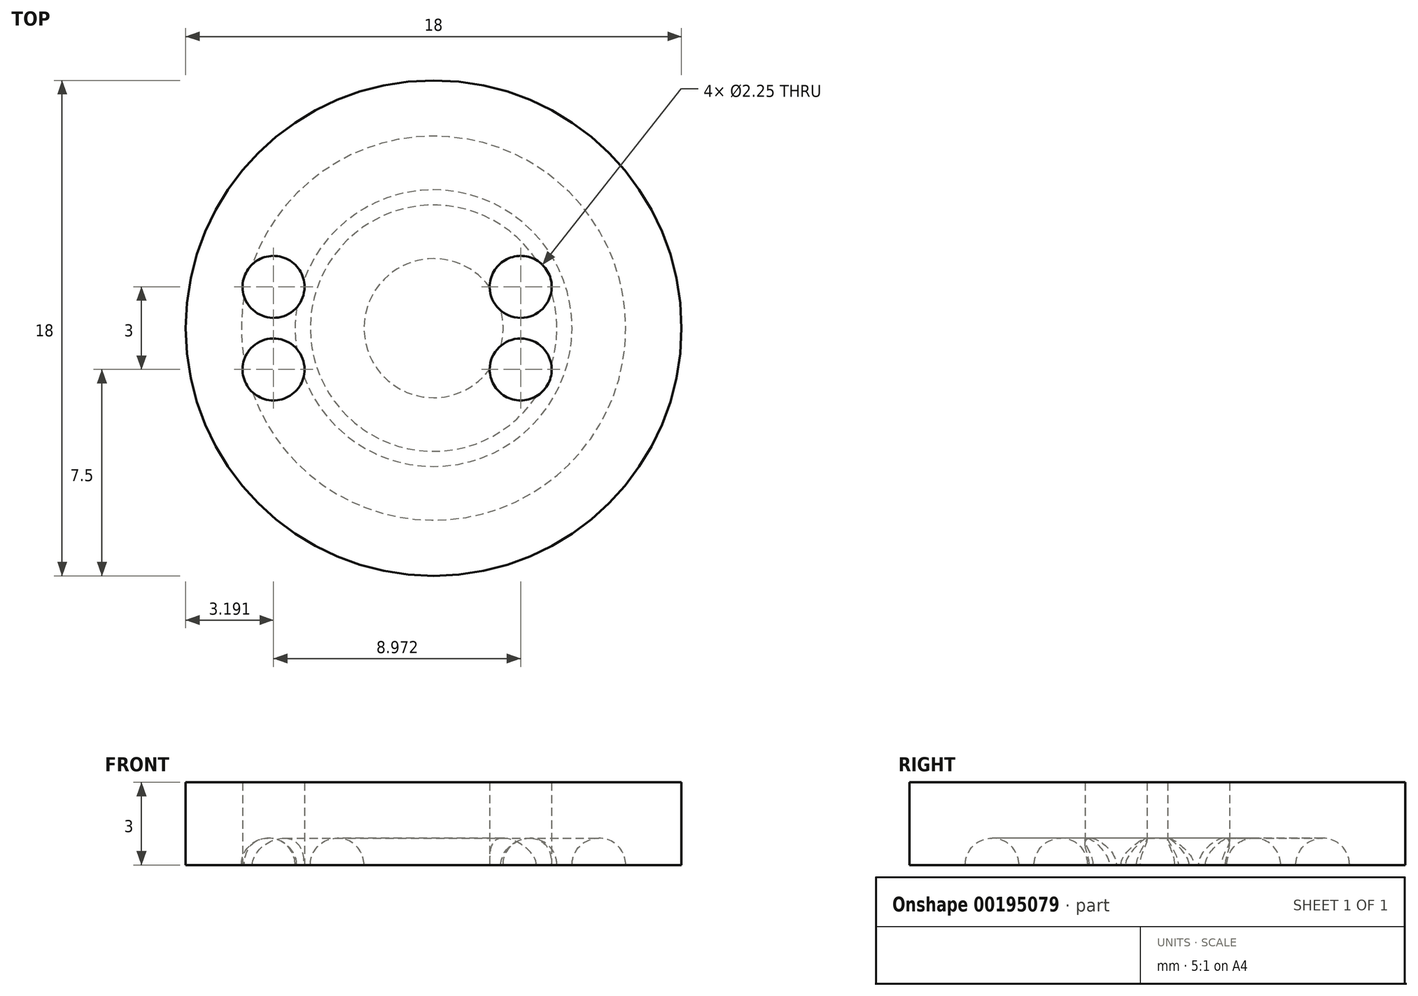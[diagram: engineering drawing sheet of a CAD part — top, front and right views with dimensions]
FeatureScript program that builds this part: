
annotation { "Feature Type Name" : "Feature", "Feature Type Description" : "" }
export const myFeature = defineFeature(function(context is Context, id is Id, definition is map)
    precondition{}
    {
        {
            assignVariable(context, id + "F0", {"name" : "thick", "anyValue" : 3});
        }
        {
            var Q0;
            Q0=qCreatedBy(makeId("Top.planeOp"),FACE);
            var sketch = newSketch(context, id + "F1", { "sketchPlane" : qUnion([Q0])});
            skCircle(sketch, "E0", {"center": v(0, 0) * mm, "radius": 9 * mm});
            skSolve(sketch);
        }
        {
            var Q0;
            Q0=qSketchRegion(id+"F1",true);
            extrude(context, id + "F2", {"entities" : qUnion([Q0]), "depth" : (getVariable(context, 'thick')) * mm});
        }
        {
            var Q0;
            Q0=makeQuery(id+"F2.opExtrude","CAP_FACE",FACE,{"disambiguationData":[OSD([sQuery(id+"F1.wireOp",EDGE,"E0")])],"isStart":true});
            var sketch = newSketch(context, id + "F3", { "sketchPlane" : qUnion([Q0])});
            skCircle(sketch, "E1", {"center": v(0, 0) * mm, "radius": 6 * mm});
            skCircle(sketch, "E2", {"center": v(0, 0) * mm, "radius": 3.5 * mm});
            skSolve(sketch);
        }
        {
            var Q0;
            Q0=qCreatedBy(makeId("Front.planeOp"),FACE);
            var sketch = newSketch(context, id + "F4", { "sketchPlane" : qUnion([Q0])});
            skCircle(sketch, "E3", {"center": v(3.5, 0) * mm, "radius": 0.97 * mm});
            skCircle(sketch, "E4", {"center": v(6, 0) * mm, "radius": 0.97 * mm});
            skLineSegment(sketch, "E5", {"start": v(0, 6.85) * mm, "end": v(0, -4.44) * mm, "construction": true});
            skLineSegment(sketch, "E6", {"start": v(11.67, 0) * mm, "end": v(-8.41, 0) * mm, "construction": true});
            skCircle(sketch, "E7", {"center": v(3.5, 0) * mm, "radius": 0.82 * mm, "construction": true});
            skCircle(sketch, "E8", {"center": v(6, 0) * mm, "radius": 0.82 * mm, "construction": true});
            skSolve(sketch);
        }
        {
            var Q0;
            Q0=makeQuery(id+"F4.imprint","IMPRINT",FACE,{"disambiguationData":[TD([[makeQuery(id+"F4.imprint","IMPRINT",EDGE,{"derivedFrom":sQuery(id+"F4.wireOp",EDGE,"E3")}),1.0]])]});
            var Q1;
            Q1=makeQuery(id+"F4.imprint","IMPRINT",FACE,{"disambiguationData":[TD([[makeQuery(id+"F4.imprint","IMPRINT",EDGE,{"derivedFrom":sQuery(id+"F4.wireOp",EDGE,"E4")}),1.0]])]});
            var Q2;
            Q2=sQuery(id+"F3.wireOp",EDGE,"E1");
            sweep(context, id + "F5", {"operationType" : NewBodyOperationType.REMOVE, "profiles" : qUnion([Q0, Q1]), "path" : qUnion([Q2])});
        }
        {
            var Q0;
            Q0=makeQuery(id+"F5.boolean.opBoolean","SPLIT",FACE,{"disambiguationData":[TD([makeQuery(id+"F5.opSweep","SWEPT_FACE",FACE,{"disambiguationData":[OSD([sQuery(id+"F3.wireOp",EDGE,"E1"),sQuery(id+"F4.wireOp",EDGE,"E3")])]})])],"derivedFrom":makeQuery(id+"F2.opExtrude","CAP_FACE",FACE,{"disambiguationData":[OSD([sQuery(id+"F1.wireOp",EDGE,"E0")])],"isStart":true})});
            var sketch = newSketch(context, id + "F6", { "sketchPlane" : qUnion([Q0])});
            skLineSegment(sketch, "E9", {"start": v(-12.07, 0) * mm, "end": v(12.46, 0) * mm, "construction": true});
            skLineSegment(sketch, "E10", {"start": v(0, 11.33) * mm, "end": v(0, -11.24) * mm, "construction": true});
            skLineSegment(sketch, "E11", {"start": v(-11.9, 3) * mm, "end": v(11.88, 3) * mm, "construction": true});
            skLineSegment(sketch, "E12", {"start": v(11.88, -3) * mm, "end": v(-11.43, -3) * mm, "construction": true});
            skCircle(sketch, "E13", {"center": v(0, 0) * mm, "radius": 6 * mm, "construction": true});
            skCircle(sketch, "E14", {"center": v(-5.8, 1.5) * mm, "radius": 1.13 * mm});
            skCircle(sketch, "E15", {"center": v(-5.8, -1.5) * mm, "radius": 1.13 * mm});
            skCircle(sketch, "E16", {"center": v(0, 0) * mm, "radius": 3.5 * mm, "construction": true});
            skCircle(sketch, "E17", {"center": v(3.16, 1.5) * mm, "radius": 1.13 * mm});
            skCircle(sketch, "E18", {"center": v(3.16, -1.5) * mm, "radius": 1.13 * mm});
            skSolve(sketch);
        }
        {
            var Q0;
            Q0=qSketchRegion(id+"F6",true);
            var Q1;
            Q1=makeQuery(id+"F2.opExtrude","CAP_FACE",FACE,{"disambiguationData":[OSD([sQuery(id+"F1.wireOp",EDGE,"E0")])],"isStart":false});
            extrude(context, id + "F7", {"entities" : qUnion([Q0]), "operationType" : NewBodyOperationType.REMOVE, "endBound" : BoundingType.UP_TO_SURFACE, "oppositeDirection" : true, "endBoundEntityFace" : qUnion([Q1]), "depth" : 25 * mm});
        }
    });
